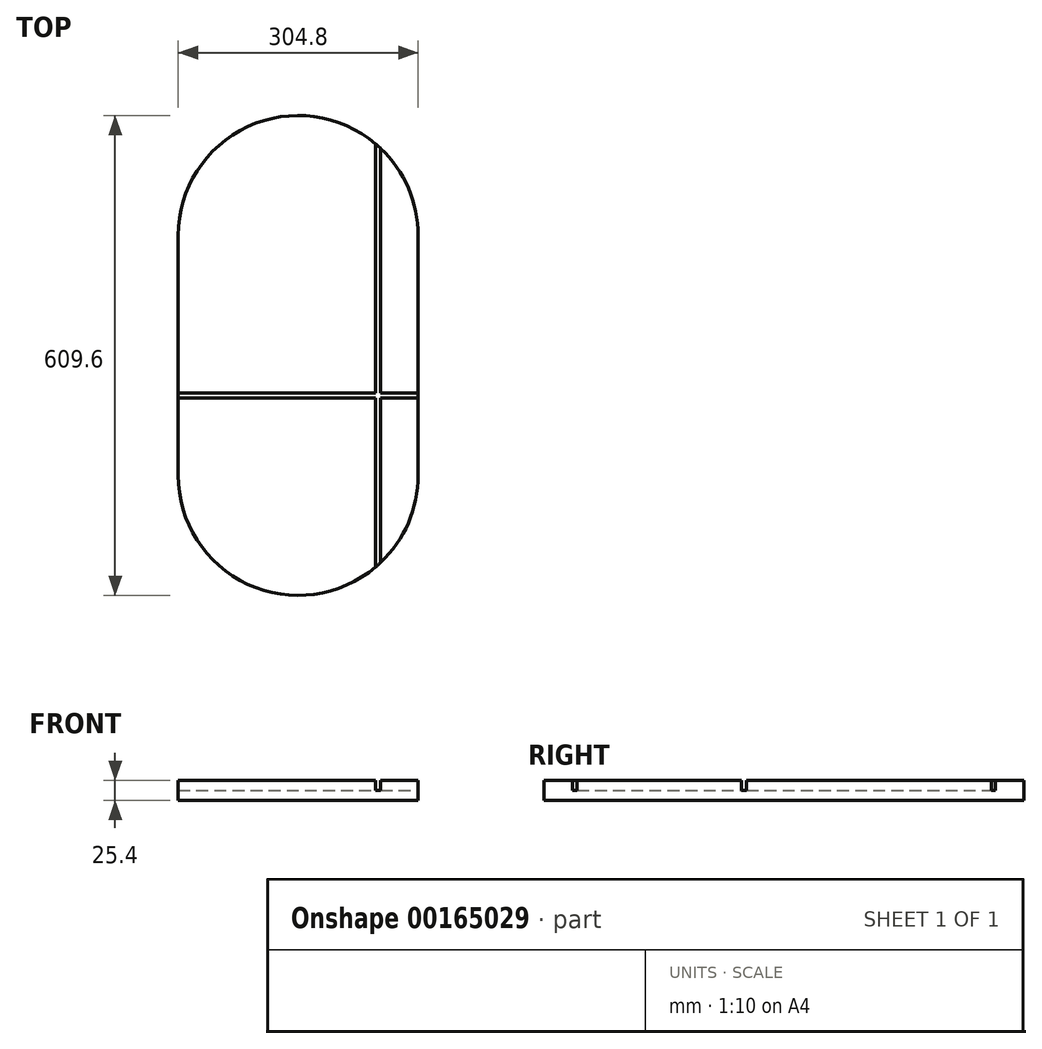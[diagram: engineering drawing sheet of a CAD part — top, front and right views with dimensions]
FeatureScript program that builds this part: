
annotation { "Feature Type Name" : "Feature", "Feature Type Description" : "" }
export const myFeature = defineFeature(function(context is Context, id is Id, definition is map)
    precondition{}
    {
        {
            var Q0;
            Q0=qCreatedBy(makeId("Top.planeOp"),FACE);
            var sketch = newSketch(context, id + "F0", { "sketchPlane" : qUnion([Q0])});
            skLineSegment(sketch, "E0.bottom", {"start": v(0, 0) * mm, "end": v(304.8, 0) * mm, "construction": true});
            skLineSegment(sketch, "E0.top", {"start": v(0, -304.8) * mm, "end": v(304.8, -304.8) * mm, "construction": true});
            skLineSegment(sketch, "E0.left", {"start": v(0, 0) * mm, "end": v(0, -304.8) * mm});
            skLineSegment(sketch, "E0.right", {"start": v(304.8, 0) * mm, "end": v(304.8, -304.8) * mm});
            skArc(sketch, "E1", {"start": v(304.8, 0) * mm, "mid": v(152.4, 152.4) * mm, "end": v(0, 0) * mm});
            skArc(sketch, "E2", {"start": v(0, -304.8) * mm, "mid": v(152.4, -457.2) * mm, "end": v(304.8, -304.8) * mm});
            skSolve(sketch);
        }
        {
            var Q0;
            Q0 = qSketchRegion(id + "F0", true);
            extrude(context, id + "F1", {"entities" : qUnion([Q0]), "depth" : 25.4 * mm});
        }
        {
            var Q0;
            Q0=makeQuery(id+"F1.opExtrude","CAP_FACE",FACE,{"disambiguationData":[OSD([sQuery(id+"F0.wireOp",EDGE,"E0.left"),sQuery(id+"F0.wireOp",EDGE,"E0.right"),sQuery(id+"F0.wireOp",EDGE,"E1"),sQuery(id+"F0.wireOp",EDGE,"E2")])],"isStart":false});
            var sketch = newSketch(context, id + "F2", { "sketchPlane" : qUnion([Q0])});
            skLineSegment(sketch, "E3", {"start": v(152.4, 0) * mm, "end": v(254, 0) * mm, "construction": true});
            skLineSegment(sketch, "E4", {"start": v(254, 0) * mm, "end": v(254, -203.2) * mm, "construction": true});
            skLineSegment(sketch, "E5.bottom", {"start": v(250.83, -421.15) * mm, "end": v(257.17, -421.15) * mm});
            skLineSegment(sketch, "E5.top", {"start": v(250.82, 116.35) * mm, "end": v(257.18, 116.35) * mm});
            skLineSegment(sketch, "E5.left", {"start": v(250.83, -421.15) * mm, "end": v(250.82, 116.35) * mm});
            skLineSegment(sketch, "E5.right", {"start": v(257.18, -421.15) * mm, "end": v(257.17, 116.35) * mm});
            skLineSegment(sketch, "E6", {"start": v(254, -203.2) * mm, "end": v(254, -421.15) * mm, "construction": true});
            skLineSegment(sketch, "E7.bottom", {"start": v(0, -200.02) * mm, "end": v(304.8, -200.02) * mm});
            skLineSegment(sketch, "E7.top", {"start": v(0, -206.38) * mm, "end": v(304.8, -206.38) * mm});
            skLineSegment(sketch, "E7.left", {"start": v(0, -200.02) * mm, "end": v(0, -206.38) * mm});
            skLineSegment(sketch, "E7.right", {"start": v(304.8, -200.02) * mm, "end": v(304.8, -206.38) * mm});
            skLineSegment(sketch, "E8", {"start": v(254, -203.2) * mm, "end": v(304.8, -203.2) * mm, "construction": true});
            skSolve(sketch);
        }
        {
            var Q0;
            Q0 = qSketchRegion(id + "F2", true);
            extrude(context, id + "F3", {"entities" : qUnion([Q0]), "operationType" : NewBodyOperationType.REMOVE, "oppositeDirection" : true, "depth" : 12.7 * mm});
        }
    });
